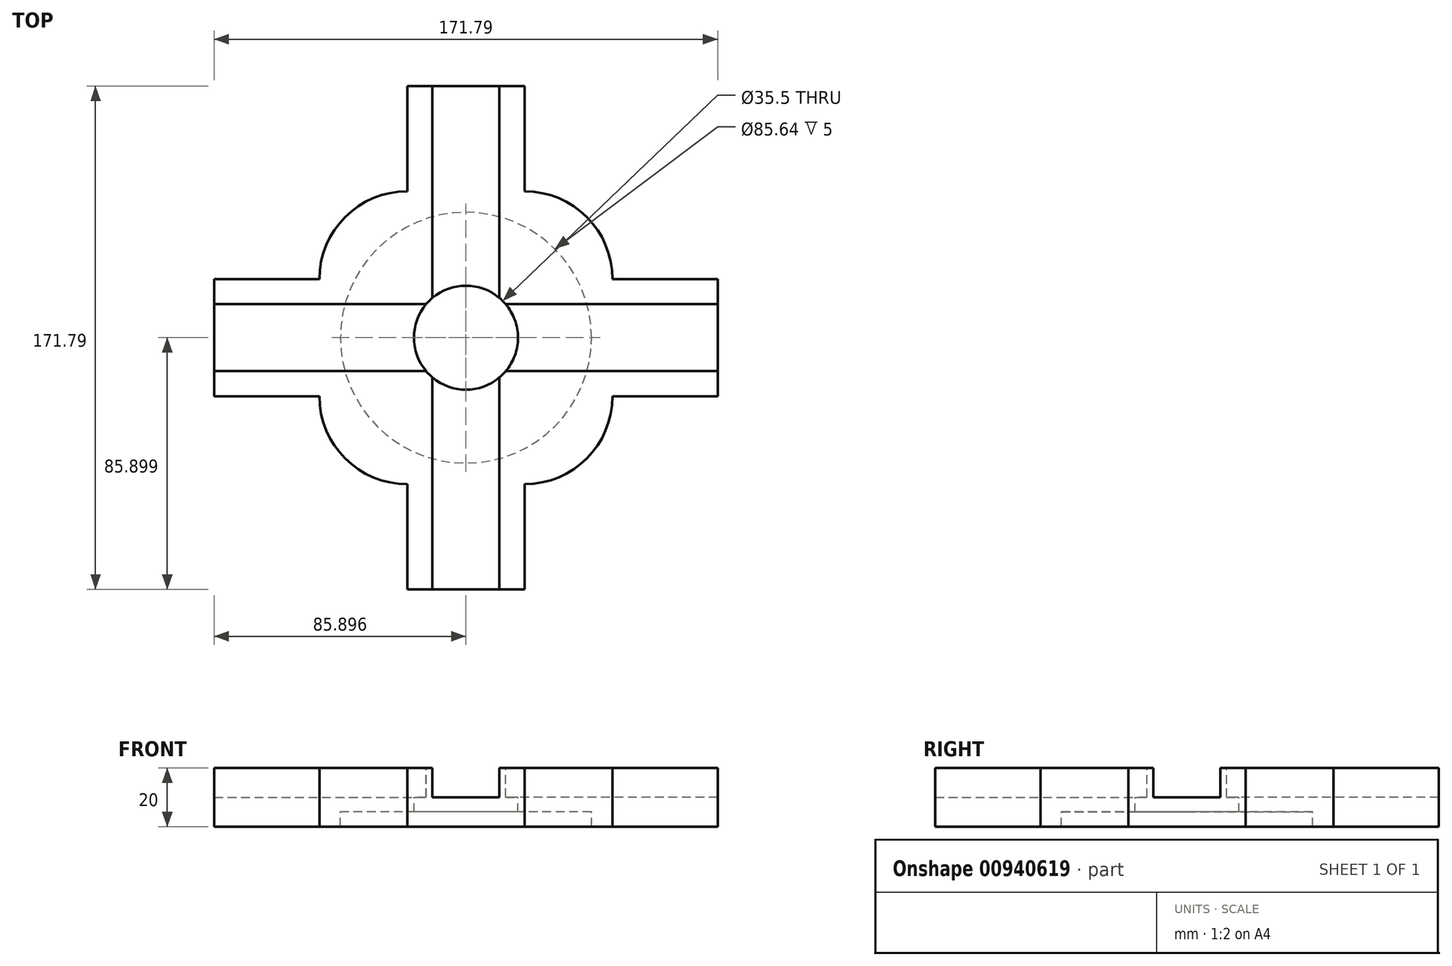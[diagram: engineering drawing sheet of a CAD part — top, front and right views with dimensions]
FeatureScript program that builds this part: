
annotation { "Feature Type Name" : "Feature", "Feature Type Description" : "" }
export const myFeature = defineFeature(function(context is Context, id is Id, definition is map)
    precondition{}
    {
        {
            var Q0;
            Q0=qCreatedBy(makeId("Top.planeOp"),FACE);
            var sketch = newSketch(context, id + "F0", { "sketchPlane" : qUnion([Q0])});
            skLineSegment(sketch, "E0.bottom", {"start": v(-21.74, 40.05) * mm, "end": v(18.26, 40.05) * mm});
            skLineSegment(sketch, "E0.top", {"start": v(-21.74, -59.95) * mm, "end": v(18.26, -59.95) * mm});
            skLineSegment(sketch, "E0.left", {"start": v(-51.74, 10.05) * mm, "end": v(-51.74, -29.95) * mm});
            skLineSegment(sketch, "E0.right", {"start": v(48.26, 10.05) * mm, "end": v(48.26, -29.95) * mm});
            skLineSegment(sketch, "E1.top", {"start": v(-21.74, 75.94) * mm, "end": v(18.26, 75.94) * mm});
            skLineSegment(sketch, "E1.left", {"start": v(-21.74, 40.05) * mm, "end": v(-21.74, 75.94) * mm});
            skLineSegment(sketch, "E1.right", {"start": v(18.26, 40.05) * mm, "end": v(18.26, 75.94) * mm});
            skLineSegment(sketch, "E2.1.0", {"start": v(-51.74, 10.05) * mm, "end": v(-87.64, 10.05) * mm});
            skLineSegment(sketch, "E2.1.1", {"start": v(-51.74, -29.95) * mm, "end": v(-87.64, -29.95) * mm});
            skLineSegment(sketch, "E2.1.2", {"start": v(-51.74, -29.95) * mm, "end": v(-51.74, 10.05) * mm});
            skLineSegment(sketch, "E2.1.3", {"start": v(-87.64, -29.95) * mm, "end": v(-87.64, 10.05) * mm});
            skLineSegment(sketch, "E2.2.0", {"start": v(-21.74, -59.95) * mm, "end": v(-21.74, -95.85) * mm});
            skLineSegment(sketch, "E2.2.1", {"start": v(18.26, -59.95) * mm, "end": v(18.26, -95.85) * mm});
            skLineSegment(sketch, "E2.2.2", {"start": v(18.26, -59.95) * mm, "end": v(-21.74, -59.95) * mm});
            skLineSegment(sketch, "E2.2.3", {"start": v(18.26, -95.85) * mm, "end": v(-21.74, -95.85) * mm});
            skLineSegment(sketch, "E2.3.0", {"start": v(48.26, -29.95) * mm, "end": v(84.15, -29.95) * mm});
            skLineSegment(sketch, "E2.3.1", {"start": v(48.26, 10.05) * mm, "end": v(84.15, 10.05) * mm});
            skLineSegment(sketch, "E2.3.3", {"start": v(84.15, 10.05) * mm, "end": v(84.15, -29.95) * mm});
            skPoint(sketch, "E2.center", {"position": v(-1.74, -9.95) * mm});
            skPoint(sketch, "E3.visualSharp", {"position": v(-51.74, 40.05) * mm});
            skArc(sketch, "E3.filletArc", {"start": v(-21.74, 40.05) * mm, "mid": v(-42.96, 31.26) * mm, "end": v(-51.74, 10.05) * mm});
            skPoint(sketch, "E4.visualSharp", {"position": v(48.26, 40.05) * mm});
            skArc(sketch, "E4.filletArc", {"start": v(48.26, 10.05) * mm, "mid": v(39.47, 31.26) * mm, "end": v(18.26, 40.05) * mm});
            skPoint(sketch, "E5.visualSharp", {"position": v(48.26, -59.95) * mm});
            skArc(sketch, "E5.filletArc", {"start": v(18.26, -59.95) * mm, "mid": v(39.47, -51.17) * mm, "end": v(48.26, -29.95) * mm});
            skPoint(sketch, "E6.visualSharp", {"position": v(-51.74, -59.95) * mm});
            skArc(sketch, "E6.filletArc", {"start": v(-51.74, -29.95) * mm, "mid": v(-42.96, -51.17) * mm, "end": v(-21.74, -59.95) * mm});
            skSolve(sketch);
        }
        {
            var Q0;
            Q0=makeQuery(id+"F0.imprint","IMPRINT",FACE,{"disambiguationData":[TD([[makeQuery(id+"F0.imprint","IMPRINT",EDGE,{"derivedFrom":sQuery(id+"F0.wireOp",EDGE,"E2.2.0")}),1.0]])]});
            var Q1;
            Q1=makeQuery(id+"F0.imprint","IMPRINT",FACE,{"disambiguationData":[TD([[makeQuery(id+"F0.imprint","IMPRINT",EDGE,{"derivedFrom":sQuery(id+"F0.wireOp",EDGE,"E0.bottom")}),-1.0]])]});
            var Q2;
            Q2=makeQuery(id+"F0.imprint","IMPRINT",FACE,{"disambiguationData":[TD([[makeQuery(id+"F0.imprint","IMPRINT",EDGE,{"derivedFrom":sQuery(id+"F0.wireOp",EDGE,"E0.right")}),1.0]])]});
            var Q3;
            Q3=makeQuery(id+"F0.imprint","IMPRINT",FACE,{"disambiguationData":[TD([[makeQuery(id+"F0.imprint","IMPRINT",EDGE,{"derivedFrom":sQuery(id+"F0.wireOp",EDGE,"E0.bottom")}),1.0]])]});
            var Q4;
            Q4=makeQuery(id+"F0.imprint","IMPRINT",FACE,{"disambiguationData":[TD([[makeQuery(id+"F0.imprint","IMPRINT",EDGE,{"derivedFrom":sQuery(id+"F0.wireOp",EDGE,"E2.1.0")}),1.0]])]});
            extrude(context, id + "F1", {"entities" : qUnion([Q0, Q1, Q2, Q3, Q4]), "depth" : 20 * mm, "offsetDistance" : 25.4 * mm});
        }
        {
            var Q0;
            Q0=makeQuery(id+"F1.opExtrude","CAP_FACE",FACE,{"disambiguationData":[OSD([sQuery(id+"F0.wireOp",EDGE,"E1.top"),sQuery(id+"F0.wireOp",EDGE,"E1.left"),sQuery(id+"F0.wireOp",EDGE,"E1.right"),sQuery(id+"F0.wireOp",EDGE,"E2.1.0"),sQuery(id+"F0.wireOp",EDGE,"E2.1.1"),sQuery(id+"F0.wireOp",EDGE,"E2.1.3"),sQuery(id+"F0.wireOp",EDGE,"E2.2.0"),sQuery(id+"F0.wireOp",EDGE,"E2.2.1"),sQuery(id+"F0.wireOp",EDGE,"E2.2.3"),sQuery(id+"F0.wireOp",EDGE,"E2.3.0"),sQuery(id+"F0.wireOp",EDGE,"E2.3.1"),sQuery(id+"F0.wireOp",EDGE,"E2.3.3"),sQuery(id+"F0.wireOp",EDGE,"E3.filletArc"),sQuery(id+"F0.wireOp",EDGE,"E4.filletArc"),sQuery(id+"F0.wireOp",EDGE,"E5.filletArc"),sQuery(id+"F0.wireOp",EDGE,"E6.filletArc")])],"isStart":false});
            var sketch = newSketch(context, id + "F2", { "sketchPlane" : qUnion([Q0])});
            skCircle(sketch, "E7", {"center": v(-1.74, -9.95) * mm, "radius": 17.75 * mm});
            skLineSegment(sketch, "E8.bottom", {"start": v(-87.64, 1.47) * mm, "end": v(-9.5, 1.47) * mm});
            skLineSegment(sketch, "E8.top", {"start": v(-87.64, -21.39) * mm, "end": v(-9.5, -21.39) * mm});
            skLineSegment(sketch, "E8.right", {"start": v(-9.5, 1.47) * mm, "end": v(-9.5, -21.39) * mm});
            skLineSegment(sketch, "E9.1.0", {"start": v(-10.02, -17.7) * mm, "end": v(8.78, -17.7) * mm});
            skLineSegment(sketch, "E10.1.0", {"start": v(-13.17, -17.7) * mm, "end": v(9.69, -17.7) * mm});
            skLineSegment(sketch, "E10.1.4", {"start": v(9.69, -95.85) * mm, "end": v(9.69, -17.7) * mm});
            skLineSegment(sketch, "E10.1.5", {"start": v(-13.17, -95.85) * mm, "end": v(-13.17, -17.7) * mm});
            skLineSegment(sketch, "E10.2.0", {"start": v(6, -21.39) * mm, "end": v(6, 1.47) * mm});
            skLineSegment(sketch, "E10.2.4", {"start": v(84.15, 1.47) * mm, "end": v(6, 1.47) * mm});
            skLineSegment(sketch, "E10.2.5", {"start": v(84.15, -21.39) * mm, "end": v(6, -21.39) * mm});
            skLineSegment(sketch, "E10.3.0", {"start": v(9.69, -2.2) * mm, "end": v(-13.17, -2.2) * mm});
            skLineSegment(sketch, "E10.3.4", {"start": v(-13.17, 75.94) * mm, "end": v(-13.17, -2.2) * mm});
            skLineSegment(sketch, "E10.3.5", {"start": v(9.69, 75.94) * mm, "end": v(9.69, -2.2) * mm});
            skLineSegment(sketch, "E11", {"start": v(-13.17, -95.85) * mm, "end": v(9.69, -95.85) * mm});
            skSolve(sketch);
        }
        {
            var Q0;
            {var subQ0=sQuery(id+"F2.wireOp",EDGE,"E8.bottom");var subQ1=sQuery(id+"F2.wireOp",EDGE,"E7");var subQ2=makeQuery(id+"F2.imprint","INTERSECT",VERTEX,{"derivedFrom":[subQ1,subQ0]});Q0=makeQuery(id+"F2.imprint","IMPRINT",FACE,{"disambiguationData":[TD([[makeQuery(id+"F2.imprint","IMPRINT",EDGE,{"disambiguationData":[TD([[subQ2,-1.0]])],"derivedFrom":subQ1}),-1.0]])]});}
            var Q1;
            {var subQ0=sQuery(id+"F2.wireOp",EDGE,"E10.3.5");var subQ1=sQuery(id+"F2.wireOp",EDGE,"E7");var subQ2=makeQuery(id+"F2.imprint","INTERSECT",VERTEX,{"derivedFrom":[subQ1,subQ0]});Q1=makeQuery(id+"F2.imprint","IMPRINT",FACE,{"disambiguationData":[TD([[makeQuery(id+"F2.imprint","IMPRINT",EDGE,{"disambiguationData":[TD([[subQ2,-1.0]])],"derivedFrom":subQ1}),-1.0]])]});}
            var Q2;
            {var subQ0=sQuery(id+"F2.wireOp",EDGE,"E10.2.4");var subQ1=sQuery(id+"F2.wireOp",EDGE,"E7");var subQ2=makeQuery(id+"F2.imprint","INTERSECT",VERTEX,{"derivedFrom":[subQ1,subQ0]});Q2=makeQuery(id+"F2.imprint","IMPRINT",FACE,{"disambiguationData":[TD([[makeQuery(id+"F2.imprint","IMPRINT",EDGE,{"disambiguationData":[TD([[subQ2,1.0]])],"derivedFrom":subQ1}),-1.0]])]});}
            var Q3;
            {var subQ0=sQuery(id+"F2.wireOp",EDGE,"E10.1.5");var subQ1=sQuery(id+"F2.wireOp",EDGE,"E7");var subQ2=makeQuery(id+"F2.imprint","INTERSECT",VERTEX,{"derivedFrom":[subQ1,subQ0]});Q3=makeQuery(id+"F2.imprint","IMPRINT",FACE,{"disambiguationData":[TD([[makeQuery(id+"F2.imprint","IMPRINT",EDGE,{"disambiguationData":[TD([[subQ2,-1.0]])],"derivedFrom":subQ1}),-1.0]])]});}
            extrude(context, id + "F3", {"entities" : qUnion([Q0, Q1, Q2, Q3]), "operationType" : NewBodyOperationType.REMOVE, "oppositeDirection" : true, "depth" : 10 * mm, "offsetDistance" : 25.4 * mm});
        }
        {
            var Q0;
            Q0=makeQuery(id+"F1.opExtrude","CAP_FACE",FACE,{"disambiguationData":[OSD([sQuery(id+"F0.wireOp",EDGE,"E1.top"),sQuery(id+"F0.wireOp",EDGE,"E1.left"),sQuery(id+"F0.wireOp",EDGE,"E1.right"),sQuery(id+"F0.wireOp",EDGE,"E2.1.0"),sQuery(id+"F0.wireOp",EDGE,"E2.1.1"),sQuery(id+"F0.wireOp",EDGE,"E2.1.3"),sQuery(id+"F0.wireOp",EDGE,"E2.2.0"),sQuery(id+"F0.wireOp",EDGE,"E2.2.1"),sQuery(id+"F0.wireOp",EDGE,"E2.2.3"),sQuery(id+"F0.wireOp",EDGE,"E2.3.0"),sQuery(id+"F0.wireOp",EDGE,"E2.3.1"),sQuery(id+"F0.wireOp",EDGE,"E2.3.3"),sQuery(id+"F0.wireOp",EDGE,"E3.filletArc"),sQuery(id+"F0.wireOp",EDGE,"E4.filletArc"),sQuery(id+"F0.wireOp",EDGE,"E5.filletArc"),sQuery(id+"F0.wireOp",EDGE,"E6.filletArc")])],"isStart":false});
            var sketch = newSketch(context, id + "F4", { "sketchPlane" : qUnion([Q0])});
            skPoint(sketch, "E12.startSnap0", {"position": v(-19.5, -9.96) * mm});
            skCircle(sketch, "E13", {"center": v(-1.74, -9.95) * mm, "radius": 17.75 * mm});
            skSolve(sketch);
        }
        {
            var Q0;
            {var subQ0=sQuery(id+"F4.wireOp",EDGE,"E13");var subQ4=makeQuery(id+"F4.imprint","INTERSECT",VERTEX,{"derivedFrom":[makeQuery(id+"F3.boolean.opBoolean","COPY",EDGE,{"derivedFrom":makeQuery(id+"F3.opExtrude","CAP_EDGE",EDGE,{"disambiguationData":[OSD([sQuery(id+"F2.wireOp",EDGE,"E10.3.5")])],"isStart":true})}),subQ0]});Q0=makeQuery(id+"F4.imprint","IMPRINT",FACE,{"disambiguationData":[TD([[makeQuery(id+"F4.imprint","IMPRINT",EDGE,{"disambiguationData":[TD([[subQ4,1.0]])],"derivedFrom":subQ0}),1.0]])]});}
            extrude(context, id + "F5", {"entities" : qUnion([Q0]), "operationType" : NewBodyOperationType.REMOVE, "oppositeDirection" : true, "depth" : 15 * mm, "offsetDistance" : 25.4 * mm});
        }
        {
            var Q0;
            Q0=makeQuery(id+"F5.boolean.opBoolean","COPY",FACE,{"derivedFrom":makeQuery(id+"F5.opExtrude","CAP_FACE",FACE,{"disambiguationData":[OSD([sQuery(id+"F4.wireOp",EDGE,"E13")])],"isStart":false})});
            var sketch = newSketch(context, id + "F6", { "sketchPlane" : qUnion([Q0])});
            skCircle(sketch, "E14", {"center": v(0, -13.08) * mm, "radius": 6.18 * mm});
            skCircle(sketch, "E15", {"center": v(0.33, -11.63) * mm, "radius": 2.86 * mm});
            skCircle(sketch, "E16", {"center": v(4.47, -11.16) * mm, "radius": 2.74 * mm});
            skLineSegment(sketch, "E17", {"start": v(-5, -10.33) * mm, "end": v(-13.55, -7.78) * mm});
            skLineSegment(sketch, "E18", {"start": v(-13.55, -7.78) * mm, "end": v(-13.13, -4.48) * mm});
            skLineSegment(sketch, "E19", {"start": v(-13.13, -4.48) * mm, "end": v(-11, -1.5) * mm});
            skLineSegment(sketch, "E20", {"start": v(-11, -1.5) * mm, "end": v(-4.45, -6.21) * mm});
            skLineSegment(sketch, "E21", {"start": v(-4.45, -6.21) * mm, "end": v(-3.03, -7.7) * mm});
            skLineSegment(sketch, "E22", {"start": v(-3.03, -7.7) * mm, "end": v(-5, -10.33) * mm});
            skLineSegment(sketch, "E23", {"start": v(-1.05, -6.99) * mm, "end": v(-5.56, -3.09) * mm});
            skLineSegment(sketch, "E24", {"start": v(-5.56, -3.09) * mm, "end": v(-3.66, 0.44) * mm});
            skLineSegment(sketch, "E25", {"start": v(-3.66, 0.44) * mm, "end": v(-0.5, 1.58) * mm});
            skLineSegment(sketch, "E26", {"start": v(-0.5, 1.58) * mm, "end": v(1.73, -4.6) * mm});
            skLineSegment(sketch, "E27", {"start": v(1.73, -4.6) * mm, "end": v(1.12, -7) * mm});
            skLineSegment(sketch, "E28", {"start": v(-5.88, -15.01) * mm, "end": v(-8.35, -18.22) * mm});
            skLineSegment(sketch, "E29", {"start": v(-8.35, -18.22) * mm, "end": v(-7.64, -18.76) * mm});
            skLineSegment(sketch, "E30", {"start": v(-7.64, -18.76) * mm, "end": v(-5.48, -15.96) * mm});
            skLineSegment(sketch, "E31", {"start": v(-4.43, -17.4) * mm, "end": v(-5.1, -20.5) * mm});
            skLineSegment(sketch, "E32", {"start": v(-5.1, -20.5) * mm, "end": v(-4.3, -20.66) * mm});
            skLineSegment(sketch, "E33", {"start": v(-4.3, -20.66) * mm, "end": v(-3.74, -18.01) * mm});
            skLineSegment(sketch, "E34", {"start": v(-1.97, -18.95) * mm, "end": v(-1.97, -22.21) * mm});
            skLineSegment(sketch, "E35", {"start": v(-1.97, -22.21) * mm, "end": v(-1.24, -22.21) * mm});
            skLineSegment(sketch, "E36", {"start": v(-1.24, -22.21) * mm, "end": v(-1.24, -19.14) * mm});
            skLineSegment(sketch, "E37", {"start": v(5.85, -15.1) * mm, "end": v(8.92, -17.2) * mm});
            skLineSegment(sketch, "E38", {"start": v(8.92, -17.2) * mm, "end": v(9.36, -16.56) * mm});
            skLineSegment(sketch, "E39", {"start": v(9.36, -16.56) * mm, "end": v(6.06, -14.3) * mm});
            skLineSegment(sketch, "E40", {"start": v(6.14, -13.8) * mm, "end": v(9.8, -15.02) * mm});
            skLineSegment(sketch, "E41", {"start": v(9.8, -15.02) * mm, "end": v(9.96, -14.55) * mm});
            skLineSegment(sketch, "E42", {"start": v(9.96, -14.55) * mm, "end": v(6.18, -13.39) * mm});
            skLineSegment(sketch, "E43", {"start": v(4.11, -17.7) * mm, "end": v(4.93, -20.42) * mm});
            skLineSegment(sketch, "E44", {"start": v(4.93, -20.42) * mm, "end": v(6.91, -19.81) * mm});
            skLineSegment(sketch, "E45", {"start": v(6.91, -19.81) * mm, "end": v(4.52, -17.3) * mm});
            skPoint(sketch, "E45.endSnap0", {"position": v(4.52, -19.06) * mm});
            skSolve(sketch);
        }
        {
            var Q0;
            {var subQ0=sQuery(id+"F6.wireOp",EDGE,"E18");Q0=makeQuery(id+"F6.imprint","IMPRINT",FACE,{"disambiguationData":[TD([[makeQuery(id+"F6.imprint","IMPRINT",EDGE,{"derivedFrom":subQ0}),-1.0]])]});}
            var Q1;
            {var subQ0=sQuery(id+"F6.wireOp",EDGE,"E23");Q1=makeQuery(id+"F6.imprint","IMPRINT",FACE,{"disambiguationData":[TD([[makeQuery(id+"F6.imprint","IMPRINT",EDGE,{"derivedFrom":subQ0}),-1.0]])]});}
            var Q2;
            {var subQ6=sQuery(id+"F6.wireOp",EDGE,"E22");Q2=makeQuery(id+"F6.imprint","IMPRINT",FACE,{"disambiguationData":[TD([[makeQuery(id+"F6.imprint","IMPRINT",EDGE,{"derivedFrom":subQ6}),1.0]])]});}
            var Q3;
            {var subQ0=sQuery(id+"F6.wireOp",EDGE,"E22");Q3=makeQuery(id+"F6.imprint","IMPRINT",FACE,{"disambiguationData":[TD([[makeQuery(id+"F6.imprint","IMPRINT",EDGE,{"derivedFrom":subQ0}),-1.0]])]});}
            var Q4;
            {var subQ0=sQuery(id+"F6.wireOp",EDGE,"E28");Q4=makeQuery(id+"F6.imprint","IMPRINT",FACE,{"disambiguationData":[TD([[makeQuery(id+"F6.imprint","IMPRINT",EDGE,{"derivedFrom":subQ0}),1.0]])]});}
            var Q5;
            {var subQ0=sQuery(id+"F6.wireOp",EDGE,"E31");Q5=makeQuery(id+"F6.imprint","IMPRINT",FACE,{"disambiguationData":[TD([[makeQuery(id+"F6.imprint","IMPRINT",EDGE,{"derivedFrom":subQ0}),1.0]])]});}
            var Q6;
            {var subQ0=sQuery(id+"F6.wireOp",EDGE,"E34");Q6=makeQuery(id+"F6.imprint","IMPRINT",FACE,{"disambiguationData":[TD([[makeQuery(id+"F6.imprint","IMPRINT",EDGE,{"derivedFrom":subQ0}),1.0]])]});}
            var Q7;
            {var subQ0=sQuery(id+"F6.wireOp",EDGE,"E43");Q7=makeQuery(id+"F6.imprint","IMPRINT",FACE,{"disambiguationData":[TD([[makeQuery(id+"F6.imprint","IMPRINT",EDGE,{"derivedFrom":subQ0}),1.0]])]});}
            var Q8;
            {var subQ0=sQuery(id+"F6.wireOp",EDGE,"E37");Q8=makeQuery(id+"F6.imprint","IMPRINT",FACE,{"disambiguationData":[TD([[makeQuery(id+"F6.imprint","IMPRINT",EDGE,{"derivedFrom":subQ0}),1.0]])]});}
            var Q9;
            {var subQ0=sQuery(id+"F6.wireOp",EDGE,"E40");Q9=makeQuery(id+"F6.imprint","IMPRINT",FACE,{"disambiguationData":[TD([[makeQuery(id+"F6.imprint","IMPRINT",EDGE,{"derivedFrom":subQ0}),1.0]])]});}
            extrude(context, id + "F7", {"entities" : qUnion([Q0, Q1, Q2, Q3, Q4, Q5, Q6, Q7, Q8, Q9]), "operationType" : NewBodyOperationType.REMOVE, "oppositeDirection" : true, "depth" : 1 * mm, "offsetDistance" : 25.4 * mm});
        }
        {
            var Q0;
            Q0=makeQuery(id+"F5.boolean.opBoolean","COPY",FACE,{"derivedFrom":makeQuery(id+"F5.opExtrude","CAP_FACE",FACE,{"disambiguationData":[OSD([sQuery(id+"F4.wireOp",EDGE,"E13")])],"isStart":false})});
            var sketch = newSketch(context, id + "F8", { "sketchPlane" : qUnion([Q0])});
            skCircle(sketch, "E46", {"center": v(-1.74, -9.95) * mm, "radius": 42.82 * mm});
            skSolve(sketch);
        }
        {
            var Q0;
            Q0 = qSketchRegion(id + "F8", true);
            extrude(context, id + "F9", {"entities" : qUnion([Q0]), "operationType" : NewBodyOperationType.REMOVE, "oppositeDirection" : true, "depth" : 25.4 * mm, "offsetDistance" : 25.4 * mm});
        }
    });
